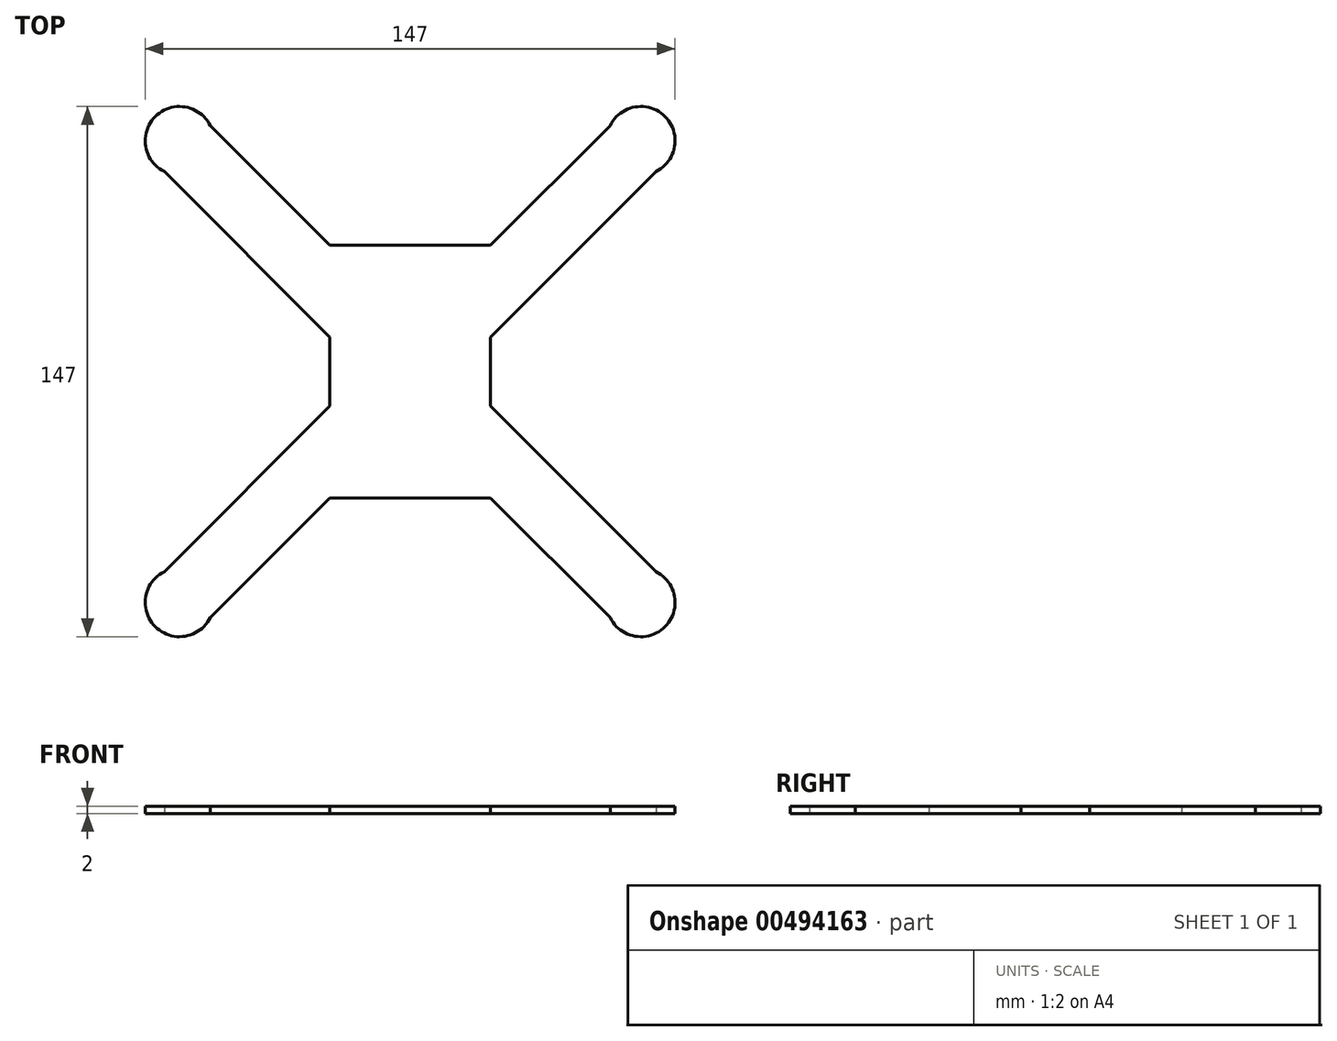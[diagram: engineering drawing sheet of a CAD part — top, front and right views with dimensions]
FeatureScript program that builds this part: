
annotation { "Feature Type Name" : "Feature", "Feature Type Description" : "" }
export const myFeature = defineFeature(function(context is Context, id is Id, definition is map)
    precondition{}
    {
        {
            var Q0;
            Q0=qCreatedBy(makeId("Top.planeOp"),FACE);
            var sketch = newSketch(context, id + "F0", { "sketchPlane" : qUnion([Q0])});
            skLineSegment(sketch, "E0", {"start": v(0, 0) * mm, "end": v(-64, 64) * mm, "construction": true});
            skArc(sketch, "E1", {"start": v(-55.49, 68.21) * mm, "mid": v(-70.72, 70.72) * mm, "end": v(-68.21, 55.49) * mm});
            skLineSegment(sketch, "E2.0", {"start": v(-22.27, 35) * mm, "end": v(-55.49, 68.21) * mm});
            skLineSegment(sketch, "E3.0", {"start": v(-22.27, 9.54) * mm, "end": v(-68.21, 55.49) * mm});
            skLineSegment(sketch, "E4.MirrorCS", {"start": v(22.27, 35) * mm, "end": v(55.49, 68.21) * mm});
            skArc(sketch, "E5.MirrorCS", {"start": v(55.49, 68.21) * mm, "mid": v(70.72, 70.72) * mm, "end": v(68.21, 55.49) * mm});
            skLineSegment(sketch, "E6.MirrorCS", {"start": v(22.27, 9.54) * mm, "end": v(68.21, 55.49) * mm});
            skLineSegment(sketch, "E7", {"start": v(22.27, 35) * mm, "end": v(-22.27, 35) * mm});
            skPoint(sketch, "E8.orphan", {"position": v(0, 12.73) * mm});
            skLineSegment(sketch, "E9", {"start": v(-22.27, 9.54) * mm, "end": v(-22.27, 0) * mm});
            skPoint(sketch, "E10.orphan", {"position": v(-12.73, 0) * mm});
            skLineSegment(sketch, "E11", {"start": v(22.27, 9.54) * mm, "end": v(22.27, 0) * mm});
            skPoint(sketch, "E12.orphan", {"position": v(12.73, 0) * mm});
            skLineSegment(sketch, "E13.MirrorCS", {"start": v(22.27, -35) * mm, "end": v(-22.27, -35) * mm});
            skLineSegment(sketch, "E14.MirrorCS", {"start": v(22.27, -35) * mm, "end": v(55.49, -68.21) * mm});
            skLineSegment(sketch, "E15.MirrorCS", {"start": v(-22.27, -35) * mm, "end": v(-55.49, -68.21) * mm});
            skArc(sketch, "E16.MirrorCS", {"start": v(-55.49, -68.21) * mm, "mid": v(-70.72, -70.72) * mm, "end": v(-68.21, -55.49) * mm});
            skArc(sketch, "E17.MirrorCS", {"start": v(55.49, -68.21) * mm, "mid": v(70.72, -70.72) * mm, "end": v(68.21, -55.49) * mm});
            skLineSegment(sketch, "E18.MirrorCS", {"start": v(-22.27, -9.54) * mm, "end": v(-68.21, -55.49) * mm});
            skLineSegment(sketch, "E19.MirrorCS", {"start": v(22.27, -9.54) * mm, "end": v(68.21, -55.49) * mm});
            skLineSegment(sketch, "E20.MirrorCS", {"start": v(22.27, -9.54) * mm, "end": v(22.27, 0) * mm});
            skLineSegment(sketch, "E21.MirrorCS", {"start": v(-22.27, -9.54) * mm, "end": v(-22.27, 0) * mm});
            skSolve(sketch);
        }
        {
            var Q0;
            Q0=qSketchRegion(id+"F0",true);
            extrude(context, id + "F1", {"entities" : qUnion([Q0]), "depth" : 2 * mm});
        }
    });
